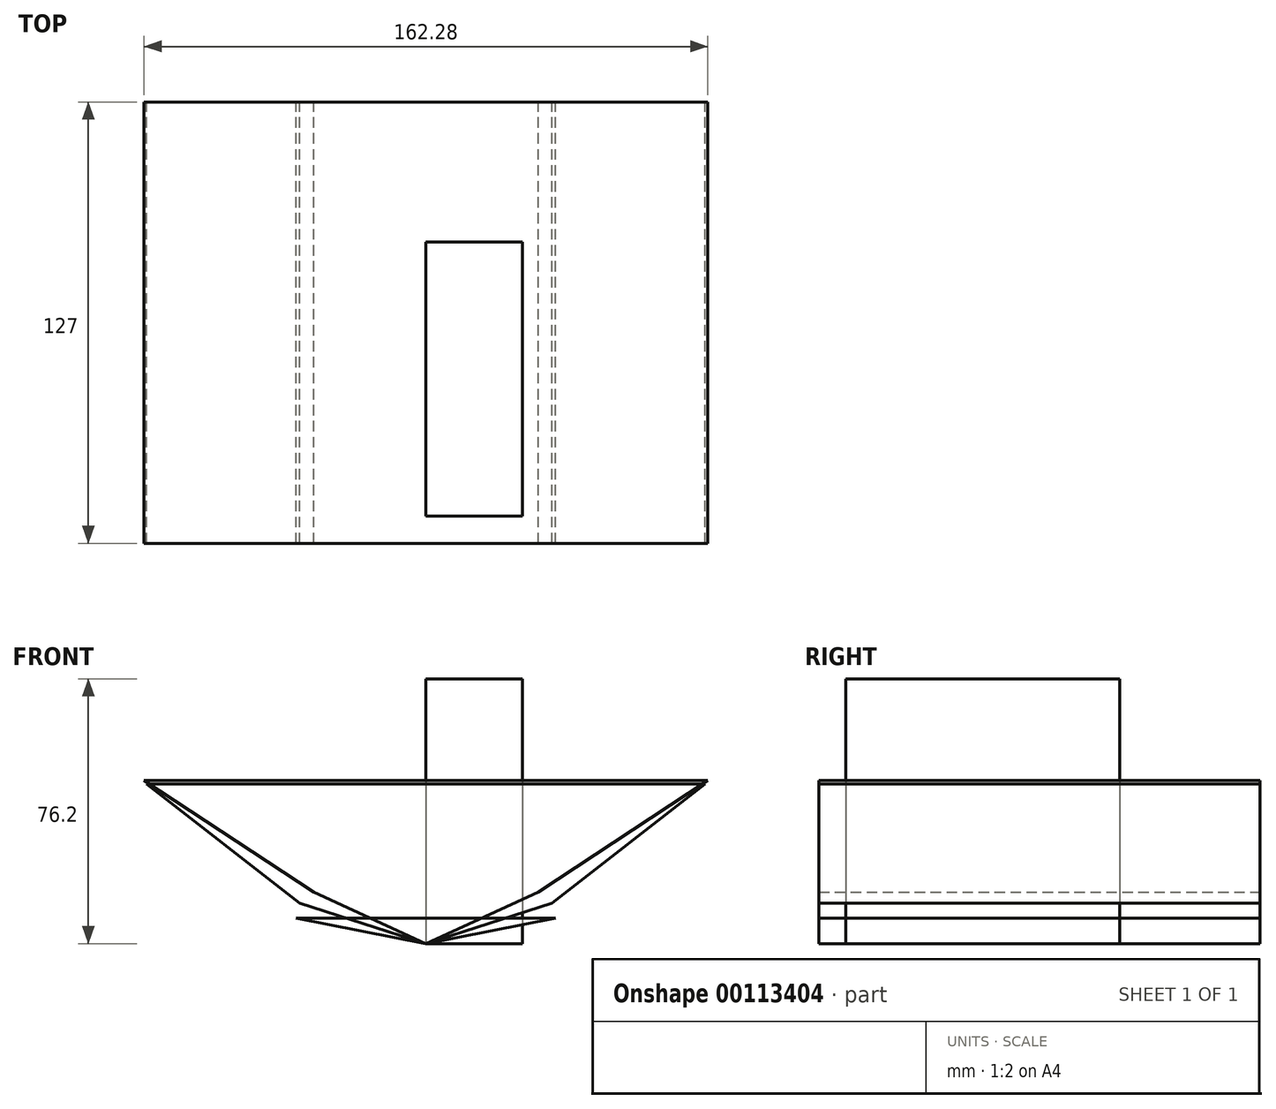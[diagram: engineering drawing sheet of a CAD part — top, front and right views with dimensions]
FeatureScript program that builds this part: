
annotation { "Feature Type Name" : "Feature", "Feature Type Description" : "" }
export const myFeature = defineFeature(function(context is Context, id is Id, definition is map)
    precondition{}
    {
        {
            var Q0;
            Q0=qCreatedBy(makeId("Front.planeOp"),FACE);
            var sketch = newSketch(context, id + "F0", { "sketchPlane" : qUnion([Q0])});
            skLineSegment(sketch, "E0", {"start": v(0, 0) * mm, "end": v(-37.39, 7.33) * mm});
            skLineSegment(sketch, "E1", {"start": v(0, 0) * mm, "end": v(37.39, 7.33) * mm});
            skLineSegment(sketch, "E2", {"start": v(37.39, 7.33) * mm, "end": v(-37.39, 7.33) * mm});
            skLineSegment(sketch, "E3", {"start": v(-37.39, 7.33) * mm, "end": v(-75.12, 41.34) * mm});
            skLineSegment(sketch, "E4", {"start": v(37.39, 7.33) * mm, "end": v(75.12, 41.34) * mm});
            skSolve(sketch);
        }
        {
            var Q0;
            Q0=qCreatedBy(makeId("Front.planeOp"),FACE);
            var sketch = newSketch(context, id + "F1", { "sketchPlane" : qUnion([Q0])});
            skLineSegment(sketch, "E5", {"start": v(0, 0) * mm, "end": v(-36.28, 11.63) * mm});
            skLineSegment(sketch, "E6", {"start": v(0, 0) * mm, "end": v(36.3, 11.6) * mm});
            skLineSegment(sketch, "E7", {"start": v(-36.28, 11.63) * mm, "end": v(-80.4, 45.93) * mm});
            skLineSegment(sketch, "E8", {"start": v(36.3, 11.6) * mm, "end": v(80.38, 45.93) * mm});
            skLineSegment(sketch, "E9", {"start": v(-80.4, 45.93) * mm, "end": v(80.38, 45.93) * mm});
            skSolve(sketch);
        }
        {
            var Q0;
            Q0=qCreatedBy(makeId("Front.planeOp"),FACE);
            var sketch = newSketch(context, id + "F2", { "sketchPlane" : qUnion([Q0])});
            skLineSegment(sketch, "E10", {"start": v(0, 0) * mm, "end": v(-32.33, 14.82) * mm});
            skLineSegment(sketch, "E11", {"start": v(-32.33, 14.82) * mm, "end": v(0, 0) * mm});
            skLineSegment(sketch, "E12", {"start": v(0, 0) * mm, "end": v(32.33, 14.82) * mm});
            skLineSegment(sketch, "E13", {"start": v(-32.33, 14.82) * mm, "end": v(32.33, 14.82) * mm});
            skLineSegment(sketch, "E14", {"start": v(-32.33, 14.82) * mm, "end": v(-81.14, 46.91) * mm});
            skLineSegment(sketch, "E15", {"start": v(32.33, 14.82) * mm, "end": v(81.14, 46.91) * mm});
            skLineSegment(sketch, "E16", {"start": v(-81.14, 46.91) * mm, "end": v(81.14, 46.91) * mm});
            skSolve(sketch);
        }
        {
            var Q0;
            Q0 = qSketchRegion(id + "F0", true);
            var Q1;
            Q1 = qSketchRegion(id + "F1", true);
            var Q2;
            Q2 = qSketchRegion(id + "F2", true);
            extrude(context, id + "F3", {"entities" : qUnion([Q0, Q1, Q2]), "depth" : 127 * mm});
        }
        {
            var Q0;
            Q0=qCreatedBy(makeId("Top.planeOp"),FACE);
            var sketch = newSketch(context, id + "F4", { "sketchPlane" : qUnion([Q0])});
            skLineSegment(sketch, "E17.bottom", {"start": v(0, -40.3) * mm, "end": v(27.8, -40.3) * mm});
            skLineSegment(sketch, "E17.top", {"start": v(0, -119.2) * mm, "end": v(27.8, -119.2) * mm});
            skLineSegment(sketch, "E17.left", {"start": v(0, -40.3) * mm, "end": v(0, -119.2) * mm});
            skLineSegment(sketch, "E17.right", {"start": v(27.8, -40.3) * mm, "end": v(27.8, -119.2) * mm});
            skSolve(sketch);
        }
        {
            var Q0;
            Q0 = qSketchRegion(id + "F4", true);
            extrude(context, id + "F5", {"entities" : qUnion([Q0]), "depth" : 76.2 * mm});
        }
    });
